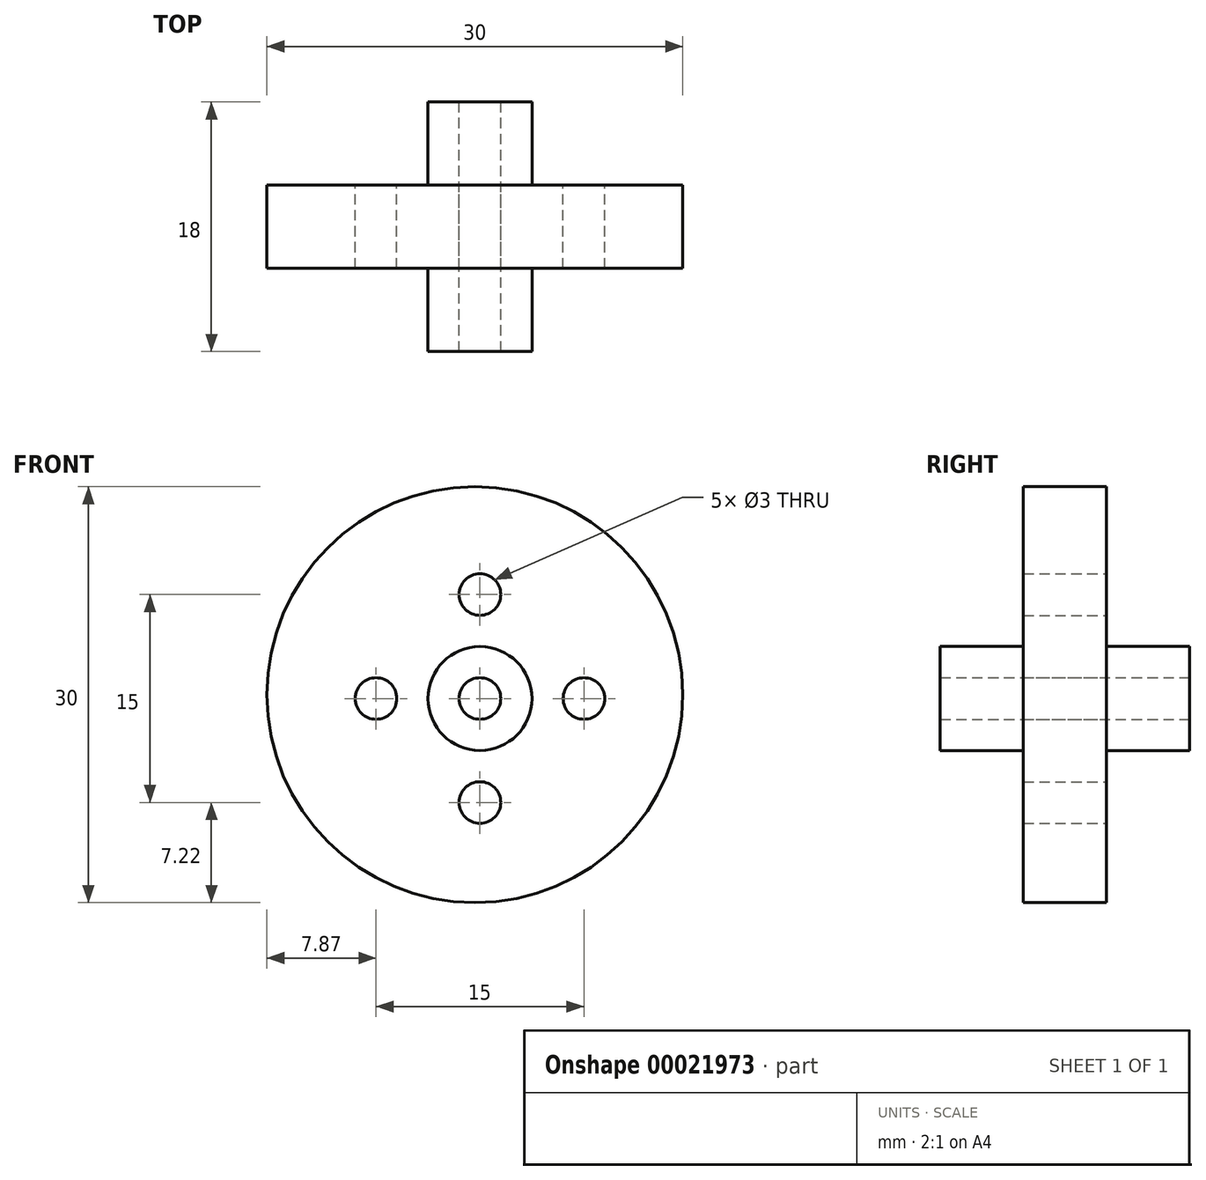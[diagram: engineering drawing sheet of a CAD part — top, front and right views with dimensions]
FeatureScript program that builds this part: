
annotation { "Feature Type Name" : "Feature", "Feature Type Description" : "" }
export const myFeature = defineFeature(function(context is Context, id is Id, definition is map)
    precondition{}
    {
        {
            var Q0;
            Q0=qCreatedBy(makeId("Front.planeOp"),FACE);
            var sketch = newSketch(context, id + "F0", { "sketchPlane" : qUnion([Q0])});
            skCircle(sketch, "E0", {"center": v(-0.37, 0.28) * mm, "radius": 15 * mm});
            skCircle(sketch, "E1", {"center": v(0, 0) * mm, "radius": 3.75 * mm});
            skCircle(sketch, "E2", {"center": v(0, 0) * mm, "radius": 1.5 * mm});
            skLineSegment(sketch, "E3", {"start": v(0, 1.5) * mm, "end": v(0, 7.5) * mm});
            skCircle(sketch, "E4", {"center": v(0, 7.5) * mm, "radius": 1.5 * mm});
            skCircle(sketch, "E5.1.0", {"center": v(-7.5, 0) * mm, "radius": 1.5 * mm});
            skCircle(sketch, "E5.2.0", {"center": v(0, -7.5) * mm, "radius": 1.5 * mm});
            skCircle(sketch, "E5.3.0", {"center": v(7.5, 0) * mm, "radius": 1.5 * mm});
            skSolve(sketch);
        }
        {
            var Q0;
            Q0=makeQuery(id+"F0.imprint","IMPRINT",FACE,{"disambiguationData":[TD([[makeQuery(id+"F0.imprint","IMPRINT",EDGE,{"derivedFrom":sQuery(id+"F0.wireOp",EDGE,"E0")}),1.0]])]});
            var Q1;
            Q1=makeQuery(id+"F0.imprint","IMPRINT",FACE,{"disambiguationData":[TD([[makeQuery(id+"F0.imprint","IMPRINT",EDGE,{"derivedFrom":sQuery(id+"F0.wireOp",EDGE,"E1")}),1.0]])]});
            extrude(context, id + "F1", {"entities" : qUnion([Q0, Q1]), "depth" : 6 * mm});
        }
        {
            var Q0;
            Q0=makeQuery(id+"F0.imprint","IMPRINT",FACE,{"disambiguationData":[TD([[makeQuery(id+"F0.imprint","IMPRINT",EDGE,{"derivedFrom":sQuery(id+"F0.wireOp",EDGE,"E1")}),1.0]])]});
            extrude(context, id + "F2", {"entities" : qUnion([Q0]), "operationType" : NewBodyOperationType.ADD, "depth" : 12 * mm});
        }
        {
            var Q0;
            Q0=makeQuery(id+"F0.imprint","IMPRINT",FACE,{"disambiguationData":[TD([[makeQuery(id+"F0.imprint","IMPRINT",EDGE,{"derivedFrom":sQuery(id+"F0.wireOp",EDGE,"E1")}),1.0]])]});
            extrude(context, id + "F3", {"entities" : qUnion([Q0]), "operationType" : NewBodyOperationType.ADD, "depth" : 6 * mm, "hasSecondDirection" : true, "secondDirectionOppositeDirection" : true, "secondDirectionDepth" : 6 * mm});
        }
    });
